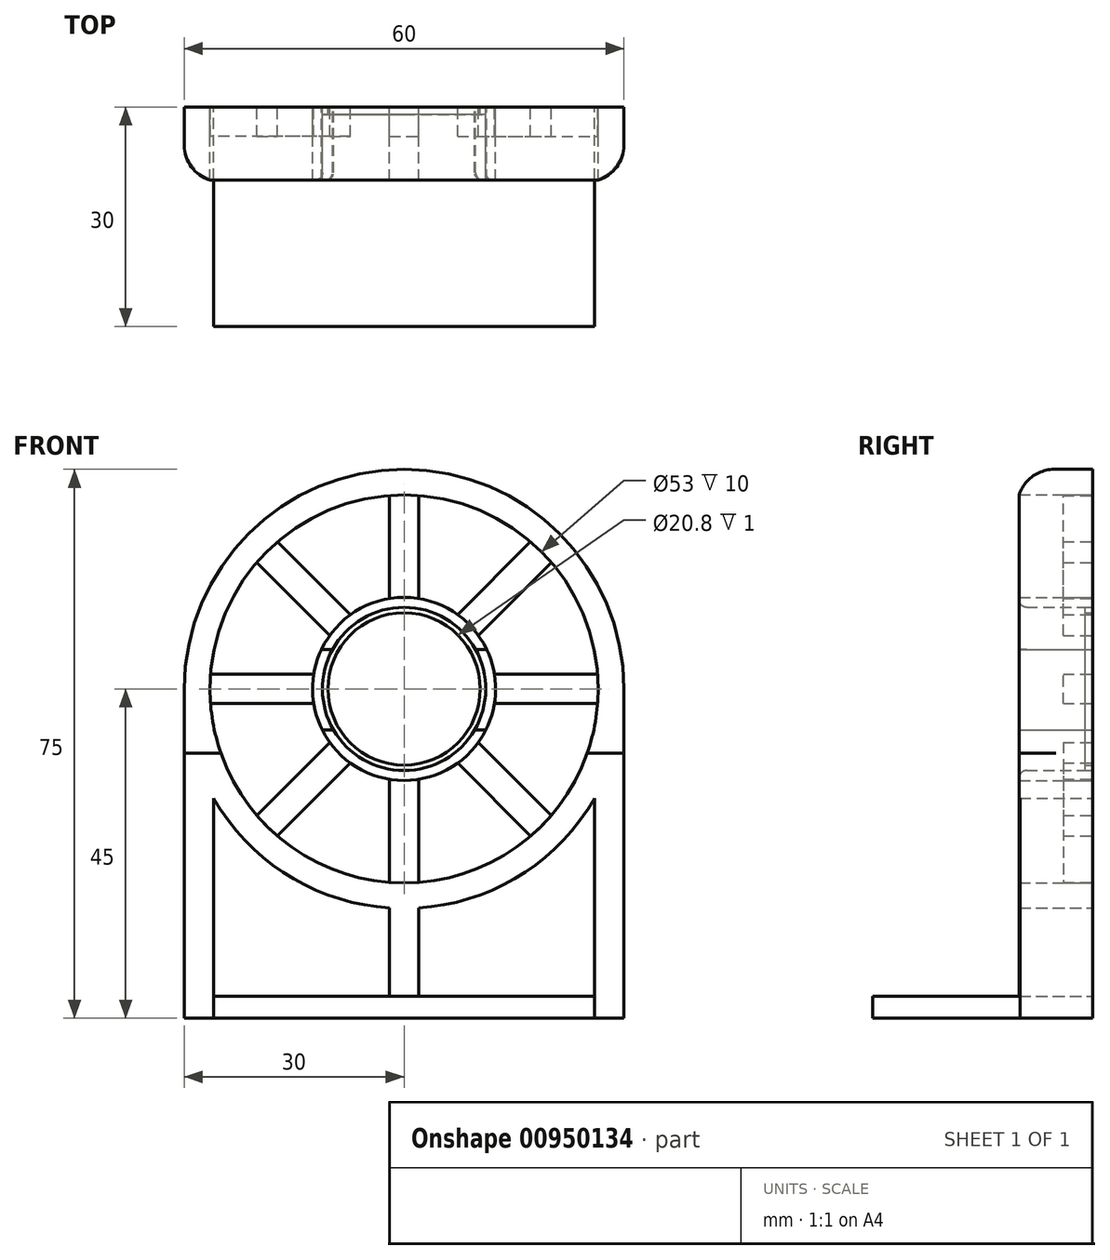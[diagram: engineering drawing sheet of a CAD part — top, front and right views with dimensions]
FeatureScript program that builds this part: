
annotation { "Feature Type Name" : "Feature", "Feature Type Description" : "" }
export const myFeature = defineFeature(function(context is Context, id is Id, definition is map)
    precondition{}
    {
        {
            var Q0;
            Q0=qCreatedBy(makeId("Front.planeOp"),FACE);
            var sketch = newSketch(context, id + "F0", { "sketchPlane" : qUnion([Q0])});
            skCircle(sketch, "E0", {"center": v(0, 0) * mm, "radius": 11.15 * mm});
            skCircle(sketch, "E1", {"center": v(0, 0) * mm, "radius": 10.4 * mm});
            skLineSegment(sketch, "E2.bottom", {"start": v(6.65, 8) * mm, "end": v(-6.65, 8) * mm});
            skLineSegment(sketch, "E2.top", {"start": v(6.65, -8) * mm, "end": v(-6.65, -8) * mm});
            skLineSegment(sketch, "E2.left", {"start": v(6.65, 8) * mm, "end": v(6.65, -8) * mm});
            skLineSegment(sketch, "E2.right", {"start": v(-6.65, 8) * mm, "end": v(-6.65, -8) * mm});
            skCircle(sketch, "E3", {"center": v(0, 0) * mm, "radius": 30 * mm});
            skCircle(sketch, "E4", {"center": v(0, 0) * mm, "radius": 26.5 * mm});
            skLineSegment(sketch, "E5", {"start": v(-30, 0) * mm, "end": v(-30, -45) * mm});
            skLineSegment(sketch, "E6", {"start": v(30, 0) * mm, "end": v(30, -45) * mm});
            skLineSegment(sketch, "E7", {"start": v(-30, -45) * mm, "end": v(30, -45) * mm});
            skLineSegment(sketch, "E8", {"start": v(-26, -45) * mm, "end": v(-26, -14.97) * mm});
            skLineSegment(sketch, "E9", {"start": v(26, -45) * mm, "end": v(26, -14.97) * mm});
            skLineSegment(sketch, "E10", {"start": v(-26, -42) * mm, "end": v(26, -42) * mm});
            skLineSegment(sketch, "E11", {"start": v(-2, -29.93) * mm, "end": v(-2, -42) * mm});
            skLineSegment(sketch, "E12", {"start": v(2, -29.93) * mm, "end": v(2, -42) * mm});
            skLineSegment(sketch, "E13", {"start": v(-8.9, 5.37) * mm, "end": v(-6.65, 5.37) * mm});
            skLineSegment(sketch, "E14", {"start": v(-6.65, 5.37) * mm, "end": v(6.65, 5.37) * mm});
            skLineSegment(sketch, "E15", {"start": v(6.65, 5.37) * mm, "end": v(8.9, 5.37) * mm});
            skLineSegment(sketch, "E16", {"start": v(8.75, -5.61) * mm, "end": v(6.65, -5.61) * mm});
            skLineSegment(sketch, "E17", {"start": v(6.65, -5.61) * mm, "end": v(-6.65, -5.61) * mm});
            skLineSegment(sketch, "E18", {"start": v(-6.65, -5.61) * mm, "end": v(-8.75, -5.61) * mm});
            skLineSegment(sketch, "E19", {"start": v(-8.9, 5.37) * mm, "end": v(-9.77, 5.37) * mm});
            skLineSegment(sketch, "E20", {"start": v(-8.75, -5.61) * mm, "end": v(-9.63, -5.61) * mm});
            skPoint(sketch, "E20.endSnap0", {"position": v(-7.7, -5.61) * mm});
            skLineSegment(sketch, "E21", {"start": v(8.75, -5.61) * mm, "end": v(9.63, -5.61) * mm});
            skLineSegment(sketch, "E22", {"start": v(8.9, 5.37) * mm, "end": v(9.77, 5.37) * mm});
            skCircle(sketch, "E23", {"center": v(0, 0) * mm, "radius": 12.5 * mm});
            skLineSegment(sketch, "E24", {"start": v(-12.34, 2) * mm, "end": v(-26.42, 2) * mm});
            skLineSegment(sketch, "E25", {"start": v(-12.34, -2) * mm, "end": v(-26.42, -2) * mm});
            skLineSegment(sketch, "E26.MirrorCS", {"start": v(12.34, 2) * mm, "end": v(26.42, 2) * mm});
            skLineSegment(sketch, "E27.MirrorCS", {"start": v(12.34, -2) * mm, "end": v(26.42, -2) * mm});
            skLineSegment(sketch, "E28", {"start": v(-2, 12.34) * mm, "end": v(-2, 26.42) * mm});
            skLineSegment(sketch, "E29", {"start": v(-2, -12.34) * mm, "end": v(-2, -26.42) * mm});
            skLineSegment(sketch, "E30.MirrorCS", {"start": v(2, 12.34) * mm, "end": v(2, 26.42) * mm});
            skLineSegment(sketch, "E31.MirrorCS", {"start": v(2, -12.34) * mm, "end": v(2, -26.42) * mm});
            skLineSegment(sketch, "E32", {"start": v(0, 0) * mm, "end": v(-18.74, 18.74) * mm});
            skLineSegment(sketch, "E33.MirrorCS", {"start": v(0, 0) * mm, "end": v(18.74, 18.74) * mm});
            skLineSegment(sketch, "E34.MirrorCS", {"start": v(0, 0) * mm, "end": v(18.74, -18.74) * mm});
            skLineSegment(sketch, "E35.MirrorCS", {"start": v(0, 0) * mm, "end": v(-18.74, -18.74) * mm});
            skLineSegment(sketch, "E36", {"start": v(-10.14, 7.31) * mm, "end": v(-20.1, 17.27) * mm});
            skLineSegment(sketch, "E37.MirrorCS", {"start": v(-7.31, 10.14) * mm, "end": v(-17.27, 20.1) * mm});
            skLineSegment(sketch, "E38.MirrorCS", {"start": v(7.31, -10.14) * mm, "end": v(17.27, -20.1) * mm});
            skLineSegment(sketch, "E39.MirrorCS", {"start": v(10.14, -7.31) * mm, "end": v(20.1, -17.27) * mm});
            skLineSegment(sketch, "E40.MirrorCS", {"start": v(10.14, 7.31) * mm, "end": v(20.1, 17.27) * mm});
            skLineSegment(sketch, "E41.MirrorCS", {"start": v(7.31, 10.14) * mm, "end": v(17.27, 20.1) * mm});
            skLineSegment(sketch, "E42.MirrorCS", {"start": v(-10.14, -7.31) * mm, "end": v(-20.1, -17.27) * mm});
            skLineSegment(sketch, "E43.MirrorCS", {"start": v(-7.31, -10.14) * mm, "end": v(-17.27, -20.1) * mm});
            skLineSegment(sketch, "E44", {"start": v(-9.77, 5.37) * mm, "end": v(-11.29, 5.37) * mm});
            skLineSegment(sketch, "E45", {"start": v(9.77, 5.37) * mm, "end": v(11.29, 5.37) * mm});
            skLineSegment(sketch, "E46", {"start": v(9.63, -5.61) * mm, "end": v(11.17, -5.61) * mm});
            skLineSegment(sketch, "E47", {"start": v(-9.63, -5.61) * mm, "end": v(-11.17, -5.61) * mm});
            skLineSegment(sketch, "E48", {"start": v(-10.96, 13.79) * mm, "end": v(-13.79, 10.96) * mm});
            skLineSegment(sketch, "E49.MirrorCS", {"start": v(10.96, 13.79) * mm, "end": v(13.79, 10.96) * mm});
            skLineSegment(sketch, "E50.MirrorCS", {"start": v(10.96, -13.79) * mm, "end": v(13.79, -10.96) * mm});
            skLineSegment(sketch, "E51.MirrorCS", {"start": v(-10.96, -13.79) * mm, "end": v(-13.79, -10.96) * mm});
            skLineSegment(sketch, "E52", {"start": v(-2, -17.5) * mm, "end": v(2, -17.5) * mm});
            skLineSegment(sketch, "E53.MirrorCS", {"start": v(-2, 17.5) * mm, "end": v(2, 17.5) * mm});
            skLineSegment(sketch, "E54.MirrorCS", {"start": v(17.5, -2) * mm, "end": v(17.5, 2) * mm});
            skLineSegment(sketch, "E55.MirrorCS", {"start": v(-17.5, 2) * mm, "end": v(-17.5, -2) * mm});
            skSolve(sketch);
        }
        {
            var Q0;
            {var subQ3=sQuery(id+"F0.wireOp",EDGE,"E33.MirrorCS");var subQ5=sQuery(id+"F0.wireOp",EDGE,"E0");var subQ6=makeQuery(id+"F0.imprint","INTERSECT",VERTEX,{"derivedFrom":[subQ5,subQ3]});Q0=makeQuery(id+"F0.imprint","IMPRINT",FACE,{"disambiguationData":[TD([[makeQuery(id+"F0.imprint","IMPRINT",EDGE,{"disambiguationData":[TD([[subQ6,-1.0]])],"derivedFrom":subQ5}),-1.0]])]});}
            var Q1;
            {var subQ2=sQuery(id+"F0.wireOp",EDGE,"E44");Q1=makeQuery(id+"F0.imprint","IMPRINT",FACE,{"disambiguationData":[TD([[makeQuery(id+"F0.imprint","IMPRINT",EDGE,{"derivedFrom":subQ2}),-1.0]])]});}
            var Q2;
            {var subQ6=sQuery(id+"F0.wireOp",EDGE,"E45");Q2=makeQuery(id+"F0.imprint","IMPRINT",FACE,{"disambiguationData":[TD([[makeQuery(id+"F0.imprint","IMPRINT",EDGE,{"derivedFrom":subQ6}),1.0]])]});}
            var Q3;
            {var subQ6=sQuery(id+"F0.wireOp",EDGE,"E46");Q3=makeQuery(id+"F0.imprint","IMPRINT",FACE,{"disambiguationData":[TD([[makeQuery(id+"F0.imprint","IMPRINT",EDGE,{"derivedFrom":subQ6}),-1.0]])]});}
            var Q4;
            {var subQ4=sQuery(id+"F0.wireOp",EDGE,"E35.MirrorCS");var subQ7=sQuery(id+"F0.wireOp",EDGE,"E0");var subQ10=makeQuery(id+"F0.imprint","INTERSECT",VERTEX,{"derivedFrom":[subQ7,subQ4]});Q4=makeQuery(id+"F0.imprint","IMPRINT",FACE,{"disambiguationData":[TD([[makeQuery(id+"F0.imprint","IMPRINT",EDGE,{"disambiguationData":[TD([[subQ10,-1.0]])],"derivedFrom":subQ7}),-1.0]])]});}
            var Q5;
            {var subQ6=sQuery(id+"F0.wireOp",EDGE,"E47");Q5=makeQuery(id+"F0.imprint","IMPRINT",FACE,{"disambiguationData":[TD([[makeQuery(id+"F0.imprint","IMPRINT",EDGE,{"derivedFrom":subQ6}),1.0]])]});}
            extrude(context, id + "F1", {"entities" : qUnion([Q0, Q1, Q2, Q3, Q4, Q5]), "depth" : 10 * mm, "offsetDistance" : 25 * mm});
        }
        {
            var Q0;
            {var subQ3=sQuery(id+"F0.wireOp",EDGE,"E44");Q0=makeQuery(id+"F0.imprint","IMPRINT",FACE,{"disambiguationData":[TD([[makeQuery(id+"F0.imprint","IMPRINT",EDGE,{"derivedFrom":subQ3}),1.0]])]});}
            var Q1;
            {var subQ4=sQuery(id+"F0.wireOp",EDGE,"E45");Q1=makeQuery(id+"F0.imprint","IMPRINT",FACE,{"disambiguationData":[TD([[makeQuery(id+"F0.imprint","IMPRINT",EDGE,{"derivedFrom":subQ4}),-1.0]])]});}
            var Q2;
            {var subQ14=sQuery(id+"F0.wireOp",EDGE,"E3");var subQ18=makeQuery(id+"F0.imprint","INTERSECT",VERTEX,{"derivedFrom":[subQ14,sQuery(id+"F0.wireOp",EDGE,"E5")]});Q2=makeQuery(id+"F0.imprint","IMPRINT",FACE,{"disambiguationData":[TD([[makeQuery(id+"F0.imprint","IMPRINT",EDGE,{"disambiguationData":[TD([[subQ18,1.0]])],"derivedFrom":subQ14}),1.0]])]});}
            var Q3;
            {var subQ1=sQuery(id+"F0.wireOp",EDGE,"E5");Q3=makeQuery(id+"F0.imprint","IMPRINT",FACE,{"disambiguationData":[TD([[makeQuery(id+"F0.imprint","IMPRINT",EDGE,{"derivedFrom":subQ1}),1.0]])]});}
            var Q4;
            {var subQ4=sQuery(id+"F0.wireOp",EDGE,"E6");Q4=makeQuery(id+"F0.imprint","IMPRINT",FACE,{"disambiguationData":[TD([[makeQuery(id+"F0.imprint","IMPRINT",EDGE,{"derivedFrom":subQ4}),-1.0]])]});}
            var Q5;
            {var subQ0=sQuery(id+"F0.wireOp",EDGE,"E11");Q5=makeQuery(id+"F0.imprint","IMPRINT",FACE,{"disambiguationData":[TD([[makeQuery(id+"F0.imprint","IMPRINT",EDGE,{"derivedFrom":subQ0}),1.0]])]});}
            extrude(context, id + "F2", {"entities" : qUnion([Q0, Q1, Q2, Q3, Q4, Q5]), "depth" : 10 * mm, "offsetDistance" : 25 * mm});
        }
        {
            var Q0;
            {var subQ1=sQuery(id+"F0.wireOp",EDGE,"E8");var subQ5=sQuery(id+"F0.wireOp",EDGE,"E7");var subQ8=makeQuery(id+"F0.imprint","INTERSECT",VERTEX,{"derivedFrom":[subQ5,subQ1]});Q0=makeQuery(id+"F0.imprint","IMPRINT",FACE,{"disambiguationData":[TD([[makeQuery(id+"F0.imprint","IMPRINT",EDGE,{"disambiguationData":[TD([[subQ8,-1.0]])],"derivedFrom":subQ5}),1.0]])]});}
            extrude(context, id + "F3", {"entities" : qUnion([Q0]), "operationType" : NewBodyOperationType.ADD, "depth" : 30 * mm, "offsetDistance" : 25 * mm});
        }
        {
            var Q0;
            {var subQ0=sQuery(id+"F0.wireOp",EDGE,"E24");Q0=makeQuery(id+"F0.imprint","IMPRINT",FACE,{"disambiguationData":[TD([[makeQuery(id+"F0.imprint","IMPRINT",EDGE,{"derivedFrom":subQ0}),1.0]])]});}
            var Q1;
            {var subQ3=sQuery(id+"F0.wireOp",EDGE,"E36");Q1=makeQuery(id+"F0.imprint","IMPRINT",FACE,{"disambiguationData":[TD([[makeQuery(id+"F0.imprint","IMPRINT",EDGE,{"derivedFrom":subQ3}),-1.0]])]});}
            var Q2;
            {var subQ3=sQuery(id+"F0.wireOp",EDGE,"E37.MirrorCS");Q2=makeQuery(id+"F0.imprint","IMPRINT",FACE,{"disambiguationData":[TD([[makeQuery(id+"F0.imprint","IMPRINT",EDGE,{"derivedFrom":subQ3}),1.0]])]});}
            var Q3;
            {var subQ0=sQuery(id+"F0.wireOp",EDGE,"E28");Q3=makeQuery(id+"F0.imprint","IMPRINT",FACE,{"disambiguationData":[TD([[makeQuery(id+"F0.imprint","IMPRINT",EDGE,{"derivedFrom":subQ0}),-1.0]])]});}
            var Q4;
            {var subQ3=sQuery(id+"F0.wireOp",EDGE,"E41.MirrorCS");Q4=makeQuery(id+"F0.imprint","IMPRINT",FACE,{"disambiguationData":[TD([[makeQuery(id+"F0.imprint","IMPRINT",EDGE,{"derivedFrom":subQ3}),-1.0]])]});}
            var Q5;
            {var subQ3=sQuery(id+"F0.wireOp",EDGE,"E40.MirrorCS");Q5=makeQuery(id+"F0.imprint","IMPRINT",FACE,{"disambiguationData":[TD([[makeQuery(id+"F0.imprint","IMPRINT",EDGE,{"derivedFrom":subQ3}),1.0]])]});}
            var Q6;
            {var subQ0=sQuery(id+"F0.wireOp",EDGE,"E26.MirrorCS");Q6=makeQuery(id+"F0.imprint","IMPRINT",FACE,{"disambiguationData":[TD([[makeQuery(id+"F0.imprint","IMPRINT",EDGE,{"derivedFrom":subQ0}),-1.0]])]});}
            var Q7;
            {var subQ3=sQuery(id+"F0.wireOp",EDGE,"E39.MirrorCS");Q7=makeQuery(id+"F0.imprint","IMPRINT",FACE,{"disambiguationData":[TD([[makeQuery(id+"F0.imprint","IMPRINT",EDGE,{"derivedFrom":subQ3}),-1.0]])]});}
            var Q8;
            {var subQ3=sQuery(id+"F0.wireOp",EDGE,"E38.MirrorCS");Q8=makeQuery(id+"F0.imprint","IMPRINT",FACE,{"disambiguationData":[TD([[makeQuery(id+"F0.imprint","IMPRINT",EDGE,{"derivedFrom":subQ3}),1.0]])]});}
            var Q9;
            {var subQ0=sQuery(id+"F0.wireOp",EDGE,"E29");Q9=makeQuery(id+"F0.imprint","IMPRINT",FACE,{"disambiguationData":[TD([[makeQuery(id+"F0.imprint","IMPRINT",EDGE,{"derivedFrom":subQ0}),1.0]])]});}
            var Q10;
            {var subQ3=sQuery(id+"F0.wireOp",EDGE,"E43.MirrorCS");Q10=makeQuery(id+"F0.imprint","IMPRINT",FACE,{"disambiguationData":[TD([[makeQuery(id+"F0.imprint","IMPRINT",EDGE,{"derivedFrom":subQ3}),-1.0]])]});}
            var Q11;
            {var subQ3=sQuery(id+"F0.wireOp",EDGE,"E42.MirrorCS");Q11=makeQuery(id+"F0.imprint","IMPRINT",FACE,{"disambiguationData":[TD([[makeQuery(id+"F0.imprint","IMPRINT",EDGE,{"derivedFrom":subQ3}),1.0]])]});}
            extrude(context, id + "F4", {"entities" : qUnion([Q0, Q1, Q2, Q3, Q4, Q5, Q6, Q7, Q8, Q9, Q10, Q11]), "depth" : 4 * mm, "offsetDistance" : 25 * mm});
        }
        {
            var Q0;
            {var subQ0=sQuery(id+"F0.wireOp",EDGE,"E3");Q0=makeQuery(id+"F2.opExtrude","CAP_EDGE",EDGE,{"disambiguationData":[OSD([subQ0]),TDD([makeQuery(id+"F0.imprint","IMPRINT",EDGE,{"disambiguationData":[TD([[makeQuery(id+"F0.imprint","INTERSECT",VERTEX,{"derivedFrom":[subQ0,sQuery(id+"F0.wireOp",EDGE,"E5")]}),1.0]])],"derivedFrom":subQ0})])],"isStart":false});}
            fillet(context, id + "F5", {"entities" : qUnion([Q0]), "radius" : 5 * mm, "tangentPropagation" : true, "allowEdgeOverflow" : false});
        }
        {
            var Q0;
            {var subQ0=sQuery(id+"F0.wireOp",EDGE,"E0");var subQ1=makeQuery(id+"F0.imprint","INTERSECT",VERTEX,{"derivedFrom":[subQ0,sQuery(id+"F0.wireOp",EDGE,"E34.MirrorCS")]});var subQ2=makeQuery(id+"F0.imprint","INTERSECT",VERTEX,{"derivedFrom":[subQ0,sQuery(id+"F0.wireOp",EDGE,"E35.MirrorCS")]});Q0=makeQuery(id+"F1.opExtrude","CAP_EDGE",EDGE,{"disambiguationData":[OSD([subQ0]),TDD([makeQuery(id+"F0.imprint","IMPRINT",EDGE,{"disambiguationData":[TD([[subQ2,1.0]])],"derivedFrom":subQ0}),makeQuery(id+"F0.imprint","IMPRINT",EDGE,{"disambiguationData":[TD([[subQ2,-1.0]])],"derivedFrom":subQ0}),makeQuery(id+"F0.imprint","IMPRINT",EDGE,{"disambiguationData":[TD([[subQ1,-1.0]])],"derivedFrom":subQ0})])],"isStart":false});}
            var Q1;
            {var subQ0=sQuery(id+"F0.wireOp",EDGE,"E0");Q1=makeQuery(id+"F2.opExtrude","CAP_EDGE",EDGE,{"disambiguationData":[OSD([subQ0]),TDD([makeQuery(id+"F0.imprint","IMPRINT",EDGE,{"disambiguationData":[TD([[makeQuery(id+"F0.imprint","INTERSECT",VERTEX,{"derivedFrom":[subQ0,sQuery(id+"F0.wireOp",EDGE,"E21"),sQuery(id+"F0.wireOp",EDGE,"E46")]}),-1.0]])],"derivedFrom":subQ0})])],"isStart":false});}
            var Q2;
            {var subQ0=sQuery(id+"F0.wireOp",EDGE,"E0");var subQ1=makeQuery(id+"F0.imprint","INTERSECT",VERTEX,{"derivedFrom":[subQ0,sQuery(id+"F0.wireOp",EDGE,"E32")]});var subQ2=makeQuery(id+"F0.imprint","INTERSECT",VERTEX,{"derivedFrom":[subQ0,sQuery(id+"F0.wireOp",EDGE,"E33.MirrorCS")]});Q2=makeQuery(id+"F1.opExtrude","CAP_EDGE",EDGE,{"disambiguationData":[OSD([subQ0]),TDD([makeQuery(id+"F0.imprint","IMPRINT",EDGE,{"disambiguationData":[TD([[subQ2,1.0]])],"derivedFrom":subQ0}),makeQuery(id+"F0.imprint","IMPRINT",EDGE,{"disambiguationData":[TD([[subQ2,-1.0]])],"derivedFrom":subQ0}),makeQuery(id+"F0.imprint","IMPRINT",EDGE,{"disambiguationData":[TD([[subQ1,-1.0]])],"derivedFrom":subQ0})])],"isStart":false});}
            var Q3;
            {var subQ0=sQuery(id+"F0.wireOp",EDGE,"E0");Q3=makeQuery(id+"F2.opExtrude","CAP_EDGE",EDGE,{"disambiguationData":[OSD([subQ0]),TDD([makeQuery(id+"F0.imprint","IMPRINT",EDGE,{"disambiguationData":[TD([[makeQuery(id+"F0.imprint","INTERSECT",VERTEX,{"derivedFrom":[subQ0,sQuery(id+"F0.wireOp",EDGE,"E19"),sQuery(id+"F0.wireOp",EDGE,"E44")]}),-1.0]])],"derivedFrom":subQ0})])],"isStart":false});}
            fillet(context, id + "F6", {"entities" : qUnion([Q0, Q1, Q2, Q3]), "radius" : 1 * mm, "tangentPropagation" : true, "allowEdgeOverflow" : false});
        }
        {
            var Q0;
            {var subQ0=sQuery(id+"F0.wireOp",EDGE,"E19");Q0=makeQuery(id+"F0.imprint","IMPRINT",FACE,{"disambiguationData":[TD([[makeQuery(id+"F0.imprint","IMPRINT",EDGE,{"derivedFrom":subQ0}),1.0]])]});}
            var Q1;
            {var subQ0=sQuery(id+"F0.wireOp",EDGE,"E19");Q1=makeQuery(id+"F0.imprint","IMPRINT",FACE,{"disambiguationData":[TD([[makeQuery(id+"F0.imprint","IMPRINT",EDGE,{"derivedFrom":subQ0}),-1.0]])]});}
            var Q2;
            {var subQ4=sQuery(id+"F0.wireOp",EDGE,"E33.MirrorCS");var subQ8=sQuery(id+"F0.wireOp",EDGE,"E0");var subQ9=makeQuery(id+"F0.imprint","INTERSECT",VERTEX,{"derivedFrom":[subQ8,subQ4]});Q2=makeQuery(id+"F0.imprint","IMPRINT",FACE,{"disambiguationData":[TD([[makeQuery(id+"F0.imprint","IMPRINT",EDGE,{"disambiguationData":[TD([[subQ9,-1.0]])],"derivedFrom":subQ8}),1.0]])]});}
            var Q3;
            {var subQ0=sQuery(id+"F0.wireOp",EDGE,"E20");Q3=makeQuery(id+"F0.imprint","IMPRINT",FACE,{"disambiguationData":[TD([[makeQuery(id+"F0.imprint","IMPRINT",EDGE,{"derivedFrom":subQ0}),1.0]])]});}
            var Q4;
            {var subQ6=sQuery(id+"F0.wireOp",EDGE,"E35.MirrorCS");var subQ7=sQuery(id+"F0.wireOp",EDGE,"E0");var subQ8=makeQuery(id+"F0.imprint","INTERSECT",VERTEX,{"derivedFrom":[subQ7,subQ6]});Q4=makeQuery(id+"F0.imprint","IMPRINT",FACE,{"disambiguationData":[TD([[makeQuery(id+"F0.imprint","IMPRINT",EDGE,{"disambiguationData":[TD([[subQ8,-1.0]])],"derivedFrom":subQ7}),1.0]])]});}
            var Q5;
            {var subQ0=sQuery(id+"F0.wireOp",EDGE,"E21");Q5=makeQuery(id+"F0.imprint","IMPRINT",FACE,{"disambiguationData":[TD([[makeQuery(id+"F0.imprint","IMPRINT",EDGE,{"derivedFrom":subQ0}),-1.0]])]});}
            var Q6;
            {var subQ0=sQuery(id+"F0.wireOp",EDGE,"E21");Q6=makeQuery(id+"F0.imprint","IMPRINT",FACE,{"disambiguationData":[TD([[makeQuery(id+"F0.imprint","IMPRINT",EDGE,{"derivedFrom":subQ0}),1.0]])]});}
            var Q7;
            {var subQ0=sQuery(id+"F0.wireOp",EDGE,"E22");Q7=makeQuery(id+"F0.imprint","IMPRINT",FACE,{"disambiguationData":[TD([[makeQuery(id+"F0.imprint","IMPRINT",EDGE,{"derivedFrom":subQ0}),1.0]])]});}
            extrude(context, id + "F7", {"entities" : qUnion([Q0, Q1, Q2, Q3, Q4, Q5, Q6, Q7]), "depth" : 1 * mm, "offsetDistance" : 25 * mm});
        }
    });
